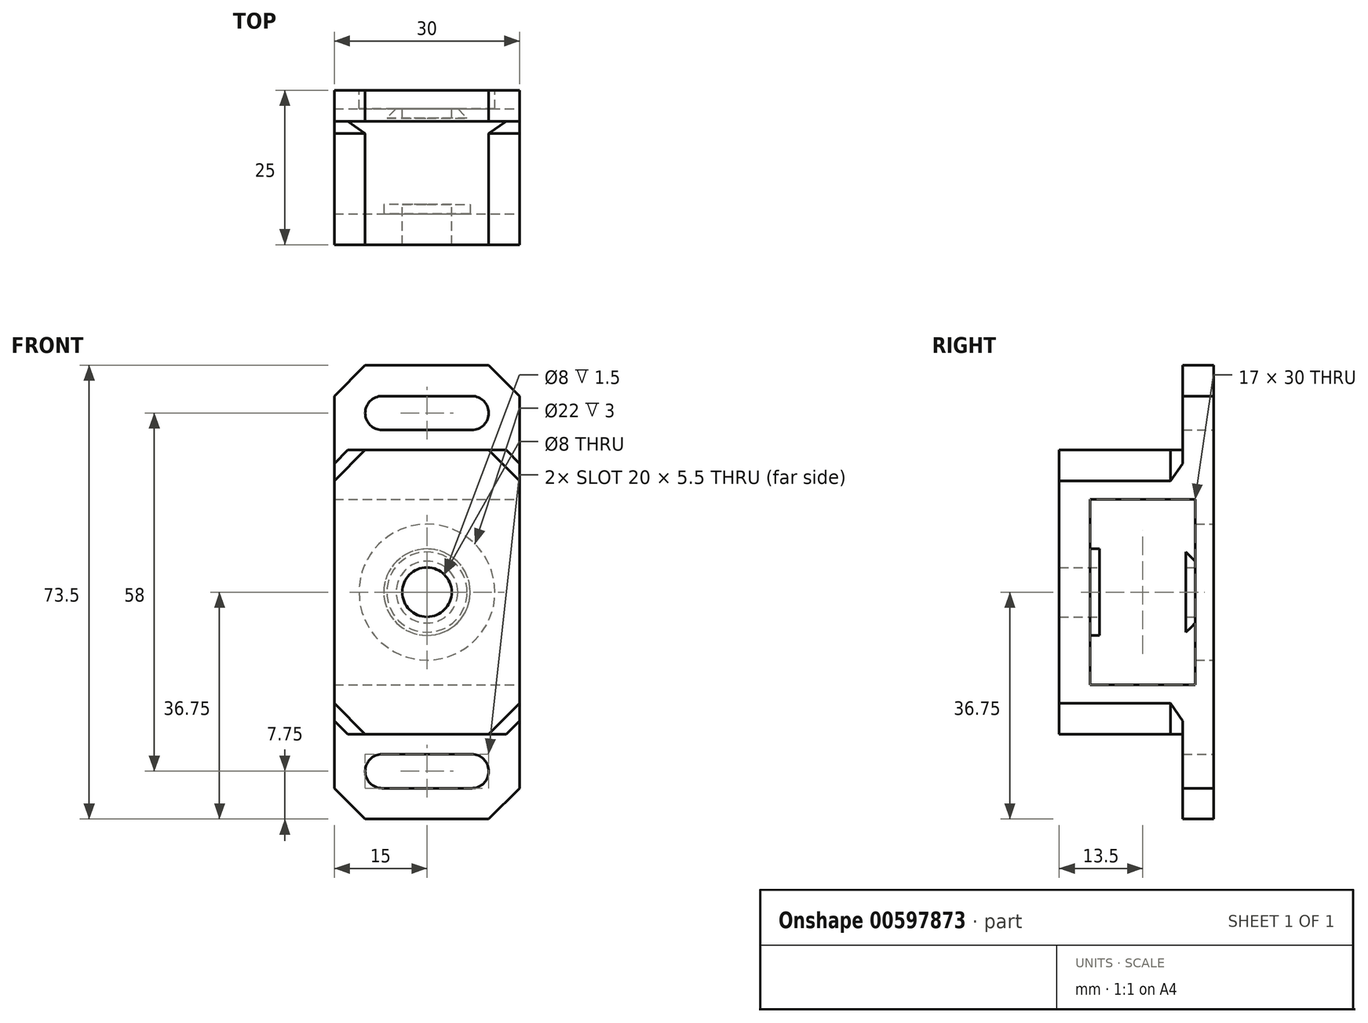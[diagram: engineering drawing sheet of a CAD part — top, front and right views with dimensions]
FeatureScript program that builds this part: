
annotation { "Feature Type Name" : "Feature", "Feature Type Description" : "" }
export const myFeature = defineFeature(function(context is Context, id is Id, definition is map)
    precondition{}
    {
        {
            var Q0;
            Q0=qCreatedBy(makeId("Front.planeOp"),FACE);
            var sketch = newSketch(context, id + "F0", { "sketchPlane" : qUnion([Q0])});
            skCircle(sketch, "E0", {"center": v(0, 0) * mm, "radius": 11 * mm});
            skCircle(sketch, "E1", {"center": v(0, 0) * mm, "radius": 4 * mm});
            skArc(sketch, "E2", {"start": v(-7.25, 31.75) * mm, "mid": v(-10, 29) * mm, "end": v(-7.25, 26.25) * mm});
            skCircle(sketch, "E3", {"center": v(0, 0) * mm, "radius": 15 * mm, "construction": true});
            skLineSegment(sketch, "E4", {"start": v(0, 0) * mm, "end": v(0, 36.75) * mm, "construction": true});
            skLineSegment(sketch, "E5.bottom", {"start": v(-15, 15) * mm, "end": v(15, 15) * mm});
            skLineSegment(sketch, "E5.top", {"start": v(-15, 23) * mm, "end": v(15, 23) * mm});
            skLineSegment(sketch, "E5.left", {"start": v(-15, 15) * mm, "end": v(-15, 23) * mm});
            skLineSegment(sketch, "E5.right", {"start": v(15, 15) * mm, "end": v(15, 23) * mm});
            skPoint(sketch, "E5.middle", {"position": v(0, 19) * mm});
            skArc(sketch, "E6", {"start": v(-1.92, 31.75) * mm, "mid": v(-13.25, 29) * mm, "end": v(-1.92, 26.25) * mm, "construction": true});
            skLineSegment(sketch, "E7", {"start": v(-15, 23) * mm, "end": v(-15, 36.75) * mm});
            skLineSegment(sketch, "E8", {"start": v(-15, 36.75) * mm, "end": v(0, 36.75) * mm});
            skPoint(sketch, "E9", {"position": v(-7.25, 31.75) * mm});
            skLineSegment(sketch, "E10", {"start": v(-7.25, 29) * mm, "end": v(-15, 29) * mm, "construction": true});
            skLineSegment(sketch, "E11", {"start": v(-7.25, 29) * mm, "end": v(-7.25, 36.75) * mm, "construction": true});
            skArc(sketch, "E12.MirrorC", {"start": v(7.25, 31.75) * mm, "mid": v(10, 29) * mm, "end": v(7.25, 26.25) * mm});
            skArc(sketch, "E13.MirrorC", {"start": v(1.92, 31.75) * mm, "mid": v(13.25, 29) * mm, "end": v(1.92, 26.25) * mm, "construction": true});
            skLineSegment(sketch, "E14.MirrorCS", {"start": v(15, 36.75) * mm, "end": v(0, 36.75) * mm});
            skLineSegment(sketch, "E15.MirrorCS", {"start": v(15, 23) * mm, "end": v(15, 36.75) * mm});
            skLineSegment(sketch, "E16", {"start": v(-7.25, 31.75) * mm, "end": v(7.25, 31.75) * mm});
            skLineSegment(sketch, "E17", {"start": v(-7.25, 26.25) * mm, "end": v(7.25, 26.25) * mm});
            skLineSegment(sketch, "E18", {"start": v(-15, 15) * mm, "end": v(-15, 0) * mm});
            skLineSegment(sketch, "E19", {"start": v(15, 15) * mm, "end": v(15, 0) * mm});
            skLineSegment(sketch, "E20", {"start": v(0, 0) * mm, "end": v(15, 0) * mm, "construction": true});
            skLineSegment(sketch, "E21.MirrorCS", {"start": v(-7.25, -29) * mm, "end": v(-7.25, -36.75) * mm, "construction": true});
            skPoint(sketch, "E22.MirrorP", {"position": v(-7.25, -31.75) * mm});
            skLineSegment(sketch, "E23.MirrorCS", {"start": v(-15, -15) * mm, "end": v(-15, 0) * mm});
            skLineSegment(sketch, "E24.MirrorCS", {"start": v(15, -15) * mm, "end": v(15, 0) * mm});
            skPoint(sketch, "E25.MirrorP", {"position": v(0, -19) * mm});
            skLineSegment(sketch, "E26.MirrorCS", {"start": v(-7.25, -29) * mm, "end": v(-15, -29) * mm, "construction": true});
            skLineSegment(sketch, "E27.MirrorCS", {"start": v(-15, -36.75) * mm, "end": v(0, -36.75) * mm});
            skLineSegment(sketch, "E28.MirrorCS", {"start": v(-7.25, -26.25) * mm, "end": v(7.25, -26.25) * mm});
            skLineSegment(sketch, "E29.MirrorCS", {"start": v(15, -36.75) * mm, "end": v(0, -36.75) * mm});
            skLineSegment(sketch, "E30.MirrorCS", {"start": v(-7.25, -31.75) * mm, "end": v(7.25, -31.75) * mm});
            skLineSegment(sketch, "E31.MirrorCS", {"start": v(-15, -15) * mm, "end": v(-15, -23) * mm});
            skLineSegment(sketch, "E32.MirrorCS", {"start": v(15, -15) * mm, "end": v(15, -23) * mm});
            skArc(sketch, "E33.MirrorCS", {"start": v(1.92, -31.75) * mm, "mid": v(13.25, -29) * mm, "end": v(1.92, -26.25) * mm, "construction": true});
            skLineSegment(sketch, "E34.MirrorCS", {"start": v(-15, -23) * mm, "end": v(15, -23) * mm});
            skLineSegment(sketch, "E35.MirrorCS", {"start": v(-15, -23) * mm, "end": v(-15, -36.75) * mm});
            skLineSegment(sketch, "E36.MirrorCS", {"start": v(15, -23) * mm, "end": v(15, -36.75) * mm});
            skArc(sketch, "E37.MirrorCS", {"start": v(-1.92, -31.75) * mm, "mid": v(-13.25, -29) * mm, "end": v(-1.92, -26.25) * mm, "construction": true});
            skLineSegment(sketch, "E38.MirrorCS", {"start": v(0, 0) * mm, "end": v(0, -36.75) * mm, "construction": true});
            skLineSegment(sketch, "E39.MirrorCS", {"start": v(-15, -15) * mm, "end": v(15, -15) * mm});
            skArc(sketch, "E40.MirrorCS", {"start": v(-7.25, -31.75) * mm, "mid": v(-10, -29) * mm, "end": v(-7.25, -26.25) * mm});
            skArc(sketch, "E41.MirrorCS", {"start": v(7.25, -31.75) * mm, "mid": v(10, -29) * mm, "end": v(7.25, -26.25) * mm});
            skSolve(sketch);
        }
        {
            var Q0;
            Q0=makeQuery(id+"F0.imprint","IMPRINT",FACE,{"disambiguationData":[TD([[makeQuery(id+"F0.imprint","IMPRINT",EDGE,{"derivedFrom":sQuery(id+"F0.wireOp",EDGE,"E5.bottom")}),-1.0]])]});
            var Q1;
            Q1=makeQuery(id+"F0.imprint","IMPRINT",FACE,{"disambiguationData":[TD([[makeQuery(id+"F0.imprint","IMPRINT",EDGE,{"derivedFrom":sQuery(id+"F0.wireOp",EDGE,"E0")}),-1.0]])]});
            extrude(context, id + "F1", {"entities" : qUnion([Q0, Q1]), "depth" : 3 * mm});
        }
        {
            var Q0;
            Q0=makeQuery(id+"F0.imprint","IMPRINT",FACE,{"disambiguationData":[TD([[makeQuery(id+"F0.imprint","IMPRINT",EDGE,{"derivedFrom":sQuery(id+"F0.wireOp",EDGE,"E5.bottom")}),1.0]])]});
            var Q1;
            Q1=makeQuery(id+"F0.imprint","IMPRINT",FACE,{"disambiguationData":[TD([[makeQuery(id+"F0.imprint","IMPRINT",EDGE,{"derivedFrom":sQuery(id+"F0.wireOp",EDGE,"E31.MirrorCS")}),1.0]])]});
            extrude(context, id + "F2", {"entities" : qUnion([Q0, Q1]), "operationType" : NewBodyOperationType.ADD, "depth" : 20 * mm});
        }
        {
            var Q0;
            Q0=makeQuery(id+"F0.imprint","IMPRINT",FACE,{"disambiguationData":[TD([[makeQuery(id+"F0.imprint","IMPRINT",EDGE,{"derivedFrom":sQuery(id+"F0.wireOp",EDGE,"E27.MirrorCS")}),1.0]])]});
            var Q1;
            Q1=makeQuery(id+"F0.imprint","IMPRINT",FACE,{"disambiguationData":[TD([[makeQuery(id+"F0.imprint","IMPRINT",EDGE,{"derivedFrom":sQuery(id+"F0.wireOp",EDGE,"E2")}),-1.0]])]});
            extrude(context, id + "F3", {"entities" : qUnion([Q0, Q1]), "operationType" : NewBodyOperationType.ADD, "depth" : 5 * mm});
        }
        {
            var Q0;
            Q0=makeQuery(id+"F2.opExtrude","CAP_FACE",FACE,{"disambiguationData":[OSD([sQuery(id+"F0.wireOp",EDGE,"E5.bottom"),sQuery(id+"F0.wireOp",EDGE,"E5.top"),sQuery(id+"F0.wireOp",EDGE,"E5.left"),sQuery(id+"F0.wireOp",EDGE,"E5.right")])],"isStart":false});
            var sketch = newSketch(context, id + "F4", { "sketchPlane" : qUnion([Q0])});
            skLineSegment(sketch, "E42.bottom", {"start": v(-15, 23) * mm, "end": v(15, 23) * mm});
            skLineSegment(sketch, "E42.top", {"start": v(-15, -23) * mm, "end": v(15, -23) * mm});
            skLineSegment(sketch, "E42.left", {"start": v(-15, 23) * mm, "end": v(-15, -23) * mm});
            skLineSegment(sketch, "E42.right", {"start": v(15, 23) * mm, "end": v(15, -23) * mm});
            skCircle(sketch, "E43", {"center": v(0, 0) * mm, "radius": 4 * mm});
            skSolve(sketch);
        }
        {
            var Q0;
            Q0=qSketchRegion(id+"F4",true);
            extrude(context, id + "F5", {"entities" : qUnion([Q0]), "operationType" : NewBodyOperationType.ADD, "depth" : 5 * mm});
        }
        {
            var Q0;
            Q0=makeQuery(id+"F1.opExtrude","CAP_FACE",FACE,{"disambiguationData":[OSD([sQuery(id+"F0.wireOp",EDGE,"E5.bottom"),sQuery(id+"F0.wireOp",EDGE,"E18"),sQuery(id+"F0.wireOp",EDGE,"E19"),sQuery(id+"F0.wireOp",EDGE,"E23.MirrorCS"),sQuery(id+"F0.wireOp",EDGE,"E24.MirrorCS"),sQuery(id+"F0.wireOp",EDGE,"E39.MirrorCS"),sQuery(id+"F0.wireOp",EDGE,"E1")])],"isStart":false});
            var sketch = newSketch(context, id + "F6", { "sketchPlane" : qUnion([Q0])});
            skCircle(sketch, "E44", {"center": v(0, 0) * mm, "radius": 7 * mm});
            skCircle(sketch, "E45", {"center": v(0, 0) * mm, "radius": 4 * mm});
            skSolve(sketch);
        }
        {
            var Q0;
            Q0=qSketchRegion(id+"F6",true);
            extrude(context, id + "F7", {"entities" : qUnion([Q0]), "operationType" : NewBodyOperationType.ADD, "depth" : 1.5 * mm});
        }
        {
            var Q0;
            Q0=makeQuery(id+"F5.opExtrude","CAP_FACE",FACE,{"disambiguationData":[OSD([sQuery(id+"F4.wireOp",EDGE,"E42.bottom"),sQuery(id+"F4.wireOp",EDGE,"E42.top"),sQuery(id+"F4.wireOp",EDGE,"E42.left"),sQuery(id+"F4.wireOp",EDGE,"E42.right"),sQuery(id+"F4.wireOp",EDGE,"E43")])],"isStart":true});
            var sketch = newSketch(context, id + "F8", { "sketchPlane" : qUnion([Q0])});
            skCircle(sketch, "E46.0", {"center": v(0, 0) * mm, "radius": 4 * mm});
            skCircle(sketch, "E46.1", {"center": v(0, 0) * mm, "radius": 7 * mm});
            skSolve(sketch);
        }
        {
            var Q0;
            Q0=qSketchRegion(id+"F8",true);
            extrude(context, id + "F9", {"entities" : qUnion([Q0]), "operationType" : NewBodyOperationType.ADD, "depth" : 1.5 * mm});
        }
        {
            var Q0;
            Q0=makeQuery(id+"F3.opExtrude","SWEPT_EDGE",EDGE,{"disambiguationData":[OSD([sQuery(id+"F0.wireOp",EDGE,"E14.MirrorCS"),sQuery(id+"F0.wireOp",EDGE,"E15.MirrorCS")])]});
            var Q1;
            Q1=makeQuery(id+"F3.opExtrude","SWEPT_EDGE",EDGE,{"disambiguationData":[OSD([sQuery(id+"F0.wireOp",EDGE,"E7"),sQuery(id+"F0.wireOp",EDGE,"E8")])]});
            var Q2;
            Q2=makeQuery(id+"F3.opExtrude","SWEPT_EDGE",EDGE,{"disambiguationData":[OSD([sQuery(id+"F0.wireOp",EDGE,"E29.MirrorCS"),sQuery(id+"F0.wireOp",EDGE,"E36.MirrorCS")])]});
            var Q3;
            Q3=makeQuery(id+"F3.opExtrude","SWEPT_EDGE",EDGE,{"disambiguationData":[OSD([sQuery(id+"F0.wireOp",EDGE,"E27.MirrorCS"),sQuery(id+"F0.wireOp",EDGE,"E35.MirrorCS")])]});
            var Q4;
            Q4=makeQuery(id+"F5.boolean.opBoolean","MERGE",EDGE,{"derivedFrom":[makeQuery(id+"F2.opExtrude","SWEPT_EDGE",EDGE,{"disambiguationData":[OSD([sQuery(id+"F0.wireOp",EDGE,"E5.top"),sQuery(id+"F0.wireOp",EDGE,"E5.left"),sQuery(id+"F0.wireOp",EDGE,"E7")])]}),makeQuery(id+"F5.opExtrude","SWEPT_EDGE",EDGE,{"disambiguationData":[OSD([sQuery(id+"F4.wireOp",EDGE,"E42.bottom"),sQuery(id+"F4.wireOp",EDGE,"E42.left")])]})]});
            var Q5;
            Q5=makeQuery(id+"F5.boolean.opBoolean","MERGE",EDGE,{"derivedFrom":[makeQuery(id+"F2.opExtrude","SWEPT_EDGE",EDGE,{"disambiguationData":[OSD([sQuery(id+"F0.wireOp",EDGE,"E5.top"),sQuery(id+"F0.wireOp",EDGE,"E5.right"),sQuery(id+"F0.wireOp",EDGE,"E15.MirrorCS")])]}),makeQuery(id+"F5.opExtrude","SWEPT_EDGE",EDGE,{"disambiguationData":[OSD([sQuery(id+"F4.wireOp",EDGE,"E42.bottom"),sQuery(id+"F4.wireOp",EDGE,"E42.right")])]})]});
            var Q6;
            Q6=makeQuery(id+"F5.boolean.opBoolean","MERGE",EDGE,{"derivedFrom":[makeQuery(id+"F2.opExtrude","SWEPT_EDGE",EDGE,{"disambiguationData":[OSD([sQuery(id+"F0.wireOp",EDGE,"E32.MirrorCS"),sQuery(id+"F0.wireOp",EDGE,"E34.MirrorCS"),sQuery(id+"F0.wireOp",EDGE,"E36.MirrorCS")])]}),makeQuery(id+"F5.opExtrude","SWEPT_EDGE",EDGE,{"disambiguationData":[OSD([sQuery(id+"F4.wireOp",EDGE,"E42.top"),sQuery(id+"F4.wireOp",EDGE,"E42.right")])]})]});
            var Q7;
            Q7=makeQuery(id+"F5.boolean.opBoolean","MERGE",EDGE,{"derivedFrom":[makeQuery(id+"F2.opExtrude","SWEPT_EDGE",EDGE,{"disambiguationData":[OSD([sQuery(id+"F0.wireOp",EDGE,"E31.MirrorCS"),sQuery(id+"F0.wireOp",EDGE,"E34.MirrorCS"),sQuery(id+"F0.wireOp",EDGE,"E35.MirrorCS")])]}),makeQuery(id+"F5.opExtrude","SWEPT_EDGE",EDGE,{"disambiguationData":[OSD([sQuery(id+"F4.wireOp",EDGE,"E42.top"),sQuery(id+"F4.wireOp",EDGE,"E42.left")])]})]});
            chamfer(context, id + "F10", {"entities" : qUnion([Q0, Q1, Q2, Q3, Q4, Q5, Q6, Q7]), "width" : 5 * mm, "tangentPropagation" : true});
        }
        {
            var Q0;
            Q0=makeQuery(id+"F7.opExtrude","CAP_EDGE",EDGE,{"disambiguationData":[OSD([sQuery(id+"F6.wireOp",EDGE,"E44")])],"isStart":true});
            var Q1;
            Q1=makeQuery(id+"F9.opExtrude","CAP_EDGE",EDGE,{"disambiguationData":[OSD([sQuery(id+"F8.wireOp",EDGE,"E46.1")])],"isStart":true});
            chamfer(context, id + "F11", {"entities" : qUnion([Q0, Q1]), "width" : 2 * mm, "tangentPropagation" : true});
        }
        {
            var Q0;
            {var subQ0=sQuery(id+"F0.wireOp",EDGE,"E15.MirrorCS");var subQ1=sQuery(id+"F0.wireOp",EDGE,"E5.top");Q0=makeQuery(id+"F10.opChamfer","BLEND_EDGE",EDGE,{"blendedFrom":[makeQuery(id+"F5.boolean.opBoolean","MERGE",EDGE,{"derivedFrom":[makeQuery(id+"F2.opExtrude","SWEPT_EDGE",EDGE,{"disambiguationData":[OSD([subQ1,sQuery(id+"F0.wireOp",EDGE,"E5.right"),subQ0])]}),makeQuery(id+"F5.opExtrude","SWEPT_EDGE",EDGE,{"disambiguationData":[OSD([sQuery(id+"F4.wireOp",EDGE,"E42.bottom"),sQuery(id+"F4.wireOp",EDGE,"E42.right")])]})]}),makeQuery(id+"F3.opExtrude","CAP_FACE",FACE,{"disambiguationData":[OSD([sQuery(id+"F0.wireOp",EDGE,"E2"),subQ1,sQuery(id+"F0.wireOp",EDGE,"E7"),sQuery(id+"F0.wireOp",EDGE,"E8"),sQuery(id+"F0.wireOp",EDGE,"E12.MirrorC"),sQuery(id+"F0.wireOp",EDGE,"E14.MirrorCS"),subQ0,sQuery(id+"F0.wireOp",EDGE,"E16"),sQuery(id+"F0.wireOp",EDGE,"E17")])],"isStart":false})],"blendedInto":[makeQuery(id+"F3.opExtrude","CAP_FACE",FACE,{"disambiguationData":[OSD([sQuery(id+"F0.wireOp",EDGE,"E2"),subQ1,sQuery(id+"F0.wireOp",EDGE,"E7"),sQuery(id+"F0.wireOp",EDGE,"E8"),sQuery(id+"F0.wireOp",EDGE,"E12.MirrorC"),sQuery(id+"F0.wireOp",EDGE,"E14.MirrorCS"),subQ0,sQuery(id+"F0.wireOp",EDGE,"E16"),sQuery(id+"F0.wireOp",EDGE,"E17")])],"isStart":false})]});}
            var Q1;
            {var subQ0=sQuery(id+"F0.wireOp",EDGE,"E7");var subQ1=sQuery(id+"F0.wireOp",EDGE,"E5.top");Q1=makeQuery(id+"F10.opChamfer","BLEND_EDGE",EDGE,{"blendedFrom":[makeQuery(id+"F5.boolean.opBoolean","MERGE",EDGE,{"derivedFrom":[makeQuery(id+"F2.opExtrude","SWEPT_EDGE",EDGE,{"disambiguationData":[OSD([subQ1,sQuery(id+"F0.wireOp",EDGE,"E5.left"),subQ0])]}),makeQuery(id+"F5.opExtrude","SWEPT_EDGE",EDGE,{"disambiguationData":[OSD([sQuery(id+"F4.wireOp",EDGE,"E42.bottom"),sQuery(id+"F4.wireOp",EDGE,"E42.left")])]})]}),makeQuery(id+"F3.opExtrude","CAP_FACE",FACE,{"disambiguationData":[OSD([sQuery(id+"F0.wireOp",EDGE,"E2"),subQ1,subQ0,sQuery(id+"F0.wireOp",EDGE,"E8"),sQuery(id+"F0.wireOp",EDGE,"E12.MirrorC"),sQuery(id+"F0.wireOp",EDGE,"E14.MirrorCS"),sQuery(id+"F0.wireOp",EDGE,"E15.MirrorCS"),sQuery(id+"F0.wireOp",EDGE,"E16"),sQuery(id+"F0.wireOp",EDGE,"E17")])],"isStart":false})],"blendedInto":[makeQuery(id+"F3.opExtrude","CAP_FACE",FACE,{"disambiguationData":[OSD([sQuery(id+"F0.wireOp",EDGE,"E2"),subQ1,subQ0,sQuery(id+"F0.wireOp",EDGE,"E8"),sQuery(id+"F0.wireOp",EDGE,"E12.MirrorC"),sQuery(id+"F0.wireOp",EDGE,"E14.MirrorCS"),sQuery(id+"F0.wireOp",EDGE,"E15.MirrorCS"),sQuery(id+"F0.wireOp",EDGE,"E16"),sQuery(id+"F0.wireOp",EDGE,"E17")])],"isStart":false})]});}
            var Q2;
            {var subQ0=sQuery(id+"F0.wireOp",EDGE,"E35.MirrorCS");var subQ1=sQuery(id+"F0.wireOp",EDGE,"E34.MirrorCS");Q2=makeQuery(id+"F10.opChamfer","BLEND_EDGE",EDGE,{"blendedFrom":[makeQuery(id+"F5.boolean.opBoolean","MERGE",EDGE,{"derivedFrom":[makeQuery(id+"F2.opExtrude","SWEPT_EDGE",EDGE,{"disambiguationData":[OSD([sQuery(id+"F0.wireOp",EDGE,"E31.MirrorCS"),subQ1,subQ0])]}),makeQuery(id+"F5.opExtrude","SWEPT_EDGE",EDGE,{"disambiguationData":[OSD([sQuery(id+"F4.wireOp",EDGE,"E42.top"),sQuery(id+"F4.wireOp",EDGE,"E42.left")])]})]}),makeQuery(id+"F3.opExtrude","CAP_FACE",FACE,{"disambiguationData":[OSD([sQuery(id+"F0.wireOp",EDGE,"E27.MirrorCS"),sQuery(id+"F0.wireOp",EDGE,"E28.MirrorCS"),sQuery(id+"F0.wireOp",EDGE,"E29.MirrorCS"),sQuery(id+"F0.wireOp",EDGE,"E30.MirrorCS"),subQ1,subQ0,sQuery(id+"F0.wireOp",EDGE,"E36.MirrorCS"),sQuery(id+"F0.wireOp",EDGE,"E40.MirrorCS"),sQuery(id+"F0.wireOp",EDGE,"E41.MirrorCS")])],"isStart":false})],"blendedInto":[makeQuery(id+"F3.opExtrude","CAP_FACE",FACE,{"disambiguationData":[OSD([sQuery(id+"F0.wireOp",EDGE,"E27.MirrorCS"),sQuery(id+"F0.wireOp",EDGE,"E28.MirrorCS"),sQuery(id+"F0.wireOp",EDGE,"E29.MirrorCS"),sQuery(id+"F0.wireOp",EDGE,"E30.MirrorCS"),subQ1,subQ0,sQuery(id+"F0.wireOp",EDGE,"E36.MirrorCS"),sQuery(id+"F0.wireOp",EDGE,"E40.MirrorCS"),sQuery(id+"F0.wireOp",EDGE,"E41.MirrorCS")])],"isStart":false})]});}
            var Q3;
            {var subQ0=sQuery(id+"F0.wireOp",EDGE,"E36.MirrorCS");var subQ1=sQuery(id+"F0.wireOp",EDGE,"E34.MirrorCS");Q3=makeQuery(id+"F10.opChamfer","BLEND_EDGE",EDGE,{"blendedFrom":[makeQuery(id+"F5.boolean.opBoolean","MERGE",EDGE,{"derivedFrom":[makeQuery(id+"F2.opExtrude","SWEPT_EDGE",EDGE,{"disambiguationData":[OSD([sQuery(id+"F0.wireOp",EDGE,"E32.MirrorCS"),subQ1,subQ0])]}),makeQuery(id+"F5.opExtrude","SWEPT_EDGE",EDGE,{"disambiguationData":[OSD([sQuery(id+"F4.wireOp",EDGE,"E42.top"),sQuery(id+"F4.wireOp",EDGE,"E42.right")])]})]}),makeQuery(id+"F3.opExtrude","CAP_FACE",FACE,{"disambiguationData":[OSD([sQuery(id+"F0.wireOp",EDGE,"E27.MirrorCS"),sQuery(id+"F0.wireOp",EDGE,"E28.MirrorCS"),sQuery(id+"F0.wireOp",EDGE,"E29.MirrorCS"),sQuery(id+"F0.wireOp",EDGE,"E30.MirrorCS"),subQ1,sQuery(id+"F0.wireOp",EDGE,"E35.MirrorCS"),subQ0,sQuery(id+"F0.wireOp",EDGE,"E40.MirrorCS"),sQuery(id+"F0.wireOp",EDGE,"E41.MirrorCS")])],"isStart":false})],"blendedInto":[makeQuery(id+"F3.opExtrude","CAP_FACE",FACE,{"disambiguationData":[OSD([sQuery(id+"F0.wireOp",EDGE,"E27.MirrorCS"),sQuery(id+"F0.wireOp",EDGE,"E28.MirrorCS"),sQuery(id+"F0.wireOp",EDGE,"E29.MirrorCS"),sQuery(id+"F0.wireOp",EDGE,"E30.MirrorCS"),subQ1,sQuery(id+"F0.wireOp",EDGE,"E35.MirrorCS"),subQ0,sQuery(id+"F0.wireOp",EDGE,"E40.MirrorCS"),sQuery(id+"F0.wireOp",EDGE,"E41.MirrorCS")])],"isStart":false})]});}
            chamfer(context, id + "F12", {"entities" : qUnion([Q0, Q1, Q2, Q3]), "width" : 2 * mm, "tangentPropagation" : true});
        }
    });
